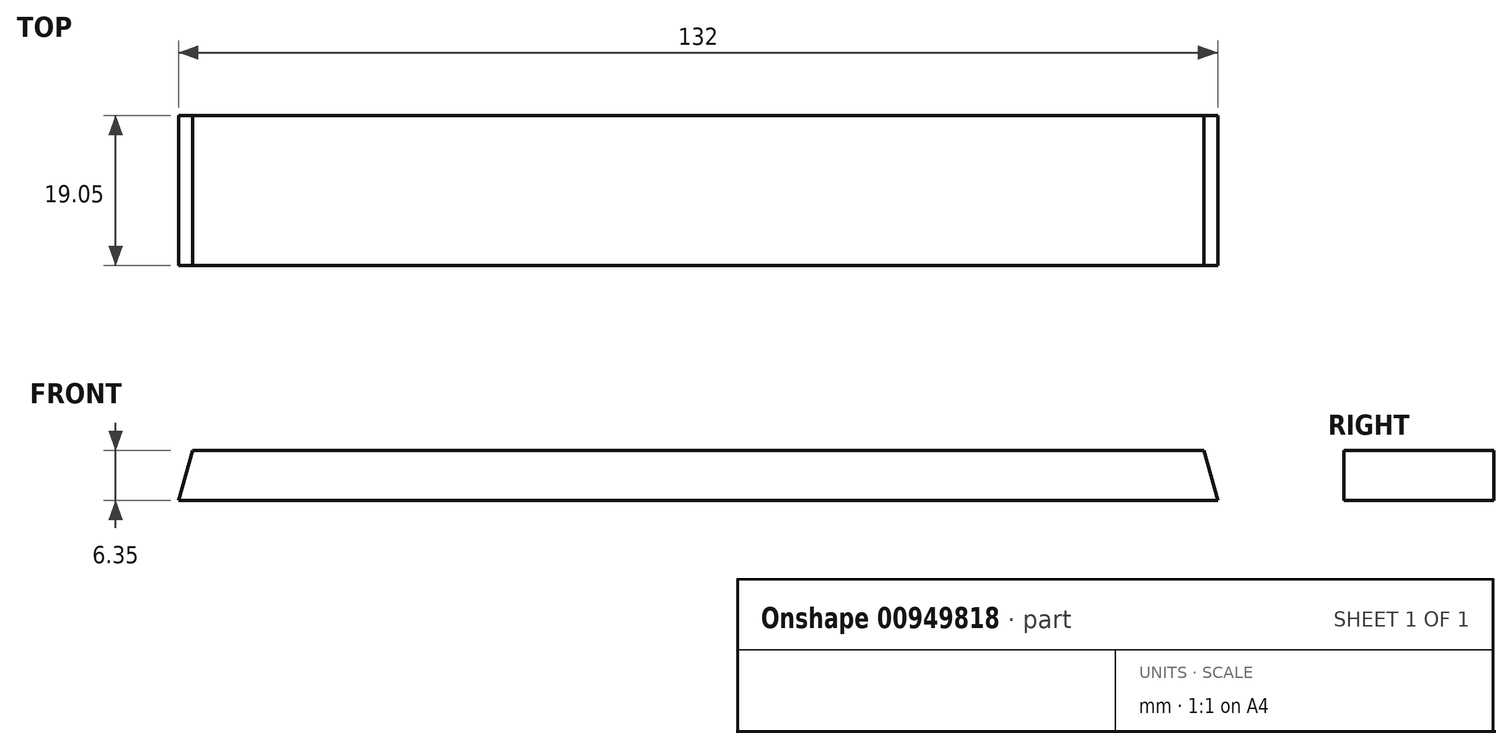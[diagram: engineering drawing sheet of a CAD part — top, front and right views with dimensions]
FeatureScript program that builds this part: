
annotation { "Feature Type Name" : "Feature", "Feature Type Description" : "" }
export const myFeature = defineFeature(function(context is Context, id is Id, definition is map)
    precondition{}
    {
        {
            var Q0;
            Q0=qCreatedBy(makeId("Front.planeOp"),FACE);
            var sketch = newSketch(context, id + "F0", { "sketchPlane" : qUnion([Q0])});
            skLineSegment(sketch, "E0", {"start": v(-63.5, 22) * mm, "end": v(63.5, 22) * mm});
            skLineSegment(sketch, "E1", {"start": v(0, 22) * mm, "end": v(0, 67.72) * mm});
            skFitSpline(sketch, "E2", {"points": [v(-63.5, 22) * mm, v(-48.61, 39.61) * mm, v(-21.13, 60.38) * mm, v(0, 67.72) * mm], "startDerivative": vector(41.59, 54.91) * mm, "endDerivative": vector(66.38, 16.65) * mm});
            skFitSpline(sketch, "E3.MirrorCS", {"points": [v(63.5, 22) * mm, v(48.61, 39.61) * mm, v(21.13, 60.38) * mm, v(0, 67.72) * mm], "startDerivative": vector(-41.59, 54.91) * mm, "endDerivative": vector(-66.38, 16.65) * mm});
            skLineSegment(sketch, "E4", {"start": v(-66, 10) * mm, "end": v(66, 10) * mm});
            skLineSegment(sketch, "E5", {"start": v(-66, 10) * mm, "end": v(-66, -80) * mm});
            skArc(sketch, "E6", {"start": v(-66, 10) * mm, "mid": v(-91.9, -35) * mm, "end": v(-66, -80) * mm});
            skArc(sketch, "E7.MirrorCS", {"start": v(66, 10) * mm, "mid": v(91.9, -35) * mm, "end": v(66, -80) * mm});
            skLineSegment(sketch, "E8", {"start": v(-63.5, 22) * mm, "end": v(-66, 10) * mm});
            skLineSegment(sketch, "E9", {"start": v(63.5, 22) * mm, "end": v(66, 10) * mm});
            skLineSegment(sketch, "E10", {"start": v(-66, -80) * mm, "end": v(66, -80) * mm});
            skSolve(sketch);
        }
        {
            var Q0;
            {var subQ2=sQuery(id+"F0.wireOp",EDGE,"E1");Q0=makeQuery(id+"F0.imprint","IMPRINT",FACE,{"disambiguationData":[TD([[makeQuery(id+"F0.imprint","IMPRINT",EDGE,{"derivedFrom":subQ2}),1.0]])]});}
            var Q1;
            {var subQ2=sQuery(id+"F0.wireOp",EDGE,"E1");Q1=makeQuery(id+"F0.imprint","IMPRINT",FACE,{"disambiguationData":[TD([[makeQuery(id+"F0.imprint","IMPRINT",EDGE,{"derivedFrom":subQ2}),-1.0]])]});}
            var Q2;
            Q2=makeQuery(id+"F0.imprint","IMPRINT",FACE,{"disambiguationData":[TD([[makeQuery(id+"F0.imprint","IMPRINT",EDGE,{"derivedFrom":sQuery(id+"F0.wireOp",EDGE,"E4")}),1.0]])]});
            var Q3;
            Q3=makeQuery(id+"F0.imprint","IMPRINT",FACE,{"disambiguationData":[TD([[makeQuery(id+"F0.imprint","IMPRINT",EDGE,{"derivedFrom":sQuery(id+"F0.wireOp",EDGE,"E5")}),-1.0]])]});
            var Q4;
            Q4=makeQuery(id+"F0.imprint","IMPRINT",FACE,{"disambiguationData":[TD([[makeQuery(id+"F0.imprint","IMPRINT",EDGE,{"derivedFrom":sQuery(id+"F0.wireOp",EDGE,"E4")}),-1.0]])]});
            extrude(context, id + "F1", {"entities" : qUnion([Q0, Q1, Q2, Q3, Q4]), "depth" : 19.05 * mm, "offsetDistance" : 25.4 * mm});
        }
        {
            var Q0;
            Q0=makeQuery(id+"F1.opExtrude","CAP_FACE",FACE,{"disambiguationData":[OSD([sQuery(id+"F0.wireOp",EDGE,"E0"),sQuery(id+"F0.wireOp",EDGE,"E2"),sQuery(id+"F0.wireOp",EDGE,"E3.MirrorCS")])],"isStart":false});
            var sketch = newSketch(context, id + "F2", { "sketchPlane" : qUnion([Q0])});
            skCircle(sketch, "E11", {"center": v(-11.95, 25.21) * mm, "radius": 1.65 * mm});
            skCircle(sketch, "E12.1.0.0", {"center": v(13.45, 25.21) * mm, "radius": 1.65 * mm});
            skLineSegment(sketch, "E12.direction1", {"start": v(-11.95, 25.21) * mm, "end": v(13.45, 25.21) * mm, "construction": true});
            skSolve(sketch);
        }
        {
            var Q0;
            Q0=makeQuery(id+"F2.imprint","IMPRINT",FACE,{"disambiguationData":[TD([[makeQuery(id+"F2.imprint","IMPRINT",EDGE,{"derivedFrom":sQuery(id+"F2.wireOp",EDGE,"E11")}),1.0]])]});
            var Q1;
            Q1=makeQuery(id+"F2.imprint","IMPRINT",FACE,{"disambiguationData":[TD([[makeQuery(id+"F2.imprint","IMPRINT",EDGE,{"derivedFrom":sQuery(id+"F2.wireOp",EDGE,"E12.1.0.0")}),1.0]])]});
            extrude(context, id + "F3", {"entities" : qUnion([Q0, Q1]), "operationType" : NewBodyOperationType.REMOVE, "oppositeDirection" : true, "depth" : 25.4 * mm, "offsetDistance" : 25.4 * mm});
        }
        {
            var Q0;
            Q0=makeQuery(id+"F1.opExtrude","CAP_FACE",FACE,{"disambiguationData":[OSD([sQuery(id+"F0.wireOp",EDGE,"E0"),sQuery(id+"F0.wireOp",EDGE,"E2"),sQuery(id+"F0.wireOp",EDGE,"E3.MirrorCS")])],"isStart":true});
            var sketch = newSketch(context, id + "F4", { "sketchPlane" : qUnion([Q0])});
            skFitSpline(sketch, "E13.0", {"points": [v(-58.44, 18.17) * mm, v(-57.57, 19.3) * mm, v(-55.86, 21.57) * mm, v(-53.68, 24.37) * mm, v(-51.87, 26.6) * mm, v(-50.46, 28.28) * mm, v(-49, 29.97) * mm, v(-47.46, 31.67) * mm, v(-46.1, 33.1) * mm, v(-44.98, 34.27) * mm, v(-44.1, 35.14) * mm, v(-43.2, 36.03) * mm, v(-41.96, 37.22) * mm, v(-40.34, 38.72) * mm, v(-38.3, 40.53) * mm, v(-36.2, 42.33) * mm, v(-34.04, 44.1) * mm, v(-31.83, 45.85) * mm, v(-29.6, 47.53) * mm, v(-27.34, 49.14) * mm, v(-25.1, 50.66) * mm, v(-22.87, 52.09) * mm, v(-21.04, 53.18) * mm, v(-19.6, 54) * mm, v(-18.73, 54.47) * mm, v(-18.03, 54.83) * mm, v(-17.34, 55.19) * mm, v(-16.48, 55.6) * mm, v(-15.47, 56.09) * mm, v(-14.12, 56.7) * mm, v(-12.45, 57.38) * mm, v(-10.47, 58.13) * mm, v(-8.5, 58.8) * mm, v(-5.87, 59.62) * mm, v(-2.56, 60.53) * mm, v(0.16, 61.21) * mm, v(1.54, 61.56) * mm]});
            skLineSegment(sketch, "E13.1", {"start": v(-60.38, 5.82) * mm, "end": v(-57.58, 19.3) * mm});
            skLineSegment(sketch, "E13.2", {"start": v(57.58, 19.3) * mm, "end": v(60.38, 5.82) * mm});
            skArc(sketch, "E13.3", {"start": v(60.38, 5.82) * mm, "mid": v(85.5, -32.8) * mm, "end": v(64.23, -73.65) * mm});
            skLineSegment(sketch, "E13.4", {"start": v(64.23, -73.65) * mm, "end": v(-64.23, -73.65) * mm});
            skFitSpline(sketch, "E13.5", {"points": [v(-1.54, 61.56) * mm, v(-0.16, 61.21) * mm, v(2.56, 60.53) * mm, v(5.87, 59.62) * mm, v(8.5, 58.8) * mm, v(10.47, 58.13) * mm, v(12.45, 57.38) * mm, v(14.12, 56.7) * mm, v(15.47, 56.09) * mm, v(16.48, 55.6) * mm, v(17.34, 55.19) * mm, v(18.03, 54.83) * mm, v(18.73, 54.47) * mm, v(19.6, 54) * mm, v(21.04, 53.18) * mm, v(22.87, 52.09) * mm, v(25.1, 50.66) * mm, v(27.34, 49.14) * mm, v(29.6, 47.53) * mm, v(31.83, 45.85) * mm, v(34.04, 44.1) * mm, v(36.2, 42.33) * mm, v(38.3, 40.53) * mm, v(40.34, 38.72) * mm, v(41.96, 37.22) * mm, v(43.2, 36.03) * mm, v(44.1, 35.14) * mm, v(44.98, 34.27) * mm, v(46.1, 33.1) * mm, v(47.46, 31.67) * mm, v(49, 29.97) * mm, v(50.46, 28.28) * mm, v(51.87, 26.6) * mm, v(53.68, 24.37) * mm, v(55.86, 21.57) * mm, v(57.57, 19.3) * mm, v(58.44, 18.17) * mm]});
            skArc(sketch, "E13.6", {"start": v(-64.23, -73.65) * mm, "mid": v(-85.5, -32.8) * mm, "end": v(-60.38, 5.82) * mm});
            skLineSegment(sketch, "E14.bottom", {"start": v(57, 22.04) * mm, "end": v(-57.58, 22.04) * mm});
            skLineSegment(sketch, "E14.top", {"start": v(57, 28.39) * mm, "end": v(-57.58, 28.39) * mm});
            skLineSegment(sketch, "E14.left", {"start": v(57, 22.04) * mm, "end": v(57, 28.39) * mm});
            skLineSegment(sketch, "E14.right", {"start": v(-57.58, 22.04) * mm, "end": v(-57.58, 28.39) * mm});
            skCircle(sketch, "E15.0", {"center": v(11.95, 25.21) * mm, "radius": 1.65 * mm});
            skLineSegment(sketch, "E16.bottom", {"start": v(8.9, 28.39) * mm, "end": v(-8.89, 28.39) * mm});
            skLineSegment(sketch, "E16.top", {"start": v(8.89, 58.66) * mm, "end": v(-8.89, 58.66) * mm});
            skLineSegment(sketch, "E16.left", {"start": v(8.9, 28.39) * mm, "end": v(8.89, 58.66) * mm});
            skLineSegment(sketch, "E16.right", {"start": v(-8.89, 28.39) * mm, "end": v(-8.89, 58.66) * mm});
            skSolve(sketch);
        }
        {
            var Q0;
            {var subQ0=sQuery(id+"F4.wireOp",EDGE,"E16.left");Q0=makeQuery(id+"F4.imprint","IMPRINT",FACE,{"disambiguationData":[TD([[makeQuery(id+"F4.imprint","IMPRINT",EDGE,{"derivedFrom":subQ0}),-1.0]])]});}
            var Q1;
            {var subQ0=sQuery(id+"F4.wireOp",EDGE,"E16.right");Q1=makeQuery(id+"F4.imprint","IMPRINT",FACE,{"disambiguationData":[TD([[makeQuery(id+"F4.imprint","IMPRINT",EDGE,{"derivedFrom":subQ0}),1.0]])]});}
            var Q2;
            {var subQ0=sQuery(id+"F4.wireOp",EDGE,"E13.1");Q2=makeQuery(id+"F4.imprint","IMPRINT",FACE,{"disambiguationData":[TD([[makeQuery(id+"F4.imprint","IMPRINT",EDGE,{"derivedFrom":subQ0}),-1.0]])]});}
            extrude(context, id + "F5", {"entities" : qUnion([Q0, Q1, Q2]), "operationType" : NewBodyOperationType.REMOVE, "oppositeDirection" : true, "depth" : 25.4 * mm, "offsetDistance" : 25.4 * mm});
        }
        {
            var Q0;
            Q0=makeQuery(id+"F4.imprint","IMPRINT",FACE,{"disambiguationData":[TD([[makeQuery(id+"F4.imprint","IMPRINT",EDGE,{"derivedFrom":sQuery(id+"F4.wireOp",EDGE,"E16.bottom")}),-1.0]])]});
            var Q1;
            Q1=makeQuery(id+"F4.imprint","IMPRINT",FACE,{"disambiguationData":[TD([[makeQuery(id+"F4.imprint","IMPRINT",EDGE,{"derivedFrom":sQuery(id+"F4.wireOp",EDGE,"E15.0")}),1.0]])]});
            extrude(context, id + "F6", {"entities" : qUnion([Q0, Q1]), "operationType" : NewBodyOperationType.REMOVE, "oppositeDirection" : true, "depth" : 15.24 * mm, "offsetDistance" : 25.4 * mm});
        }
        {
            var Q0;
            Q0=makeQuery(id+"F1.opExtrude","CAP_FACE",FACE,{"disambiguationData":[OSD([sQuery(id+"F0.wireOp",EDGE,"E0"),sQuery(id+"F0.wireOp",EDGE,"E2"),sQuery(id+"F0.wireOp",EDGE,"E3.MirrorCS")])],"isStart":false});
            var sketch = newSketch(context, id + "F7", { "sketchPlane" : qUnion([Q0])});
            skLineSegment(sketch, "E17", {"start": v(-0.56, 61.31) * mm, "end": v(-0.56, 61.31) * mm});
            skLineSegment(sketch, "E18.MirrorCS", {"start": v(0.56, 61.31) * mm, "end": v(0.56, 61.31) * mm});
            skSolve(sketch);
        }
        {
            var Q0;
            {var subQ7=sQuery(id+"F0.wireOp",EDGE,"E2");Q0=makeQuery(id+"F7.imprint","IMPRINT",FACE,{"disambiguationData":[TD([[makeQuery(id+"F7.imprint","IMPRINT",EDGE,{"derivedFrom":makeQuery(id+"F1.opExtrude","CAP_EDGE",EDGE,{"disambiguationData":[OSD([subQ7])],"isStart":false})}),-1.0]])]});}
            var sketch = newSketch(context, id + "F8", { "sketchPlane" : qUnion([Q0])});
            skPoint(sketch, "E19.0", {"position": v(-66, -80) * mm});
            skPoint(sketch, "E20.0", {"position": v(-64.23, -73.65) * mm});
            skPoint(sketch, "E21.0", {"position": v(64.23, -73.65) * mm});
            skPoint(sketch, "E22.0", {"position": v(66, -80) * mm});
            skLineSegment(sketch, "E23.0", {"start": v(-64.23, -73.65) * mm, "end": v(64.23, -73.65) * mm});
            skLineSegment(sketch, "E24.0", {"start": v(-66, -80) * mm, "end": v(66, -80) * mm});
            skLineSegment(sketch, "E25", {"start": v(-64.23, -73.65) * mm, "end": v(-66, -80) * mm});
            skLineSegment(sketch, "E26", {"start": v(64.23, -73.65) * mm, "end": v(66, -80) * mm});
            skSolve(sketch);
        }
        {
            var Q0;
            Q0=makeQuery(id+"F8.imprint","IMPRINT",FACE,{"disambiguationData":[TD([[makeQuery(id+"F8.imprint","IMPRINT",EDGE,{"derivedFrom":sQuery(id+"F8.wireOp",EDGE,"E23.0")}),1.0]])]});
            extrude(context, id + "F9", {"entities" : qUnion([Q0]), "operationType" : NewBodyOperationType.REMOVE, "oppositeDirection" : true, "depth" : 25.4 * mm, "offsetDistance" : 25.4 * mm});
        }
    });
